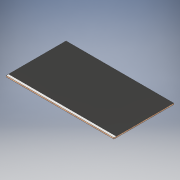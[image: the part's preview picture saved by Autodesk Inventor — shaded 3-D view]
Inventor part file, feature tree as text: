
AUTODESK INVENTOR PART (.ipt)
format: ipt  version: 2017 (Build 210142000, 142)  size: 102,400 bytes
history: native  units: in
note: dims shown in document units (in); Inventor stores cm internally (conversion verified against a paired STEP export)
features: extrude x2, sketch x2
ambient origin geometry x8: Origin, YZ Plane, XZ Plane, XY Plane, X Axis, Y Axis, Z Axis, Center Point
bodies: Solid1 (feature_tree)
feature tree (4):
  extrude  "Extrusion1"  Depth=25.0in
  extrude  "Extrusion2"  Depth=1.0in
  sketch  "Sketch1"  dims[d0=45.0in d1=25.0in]
  sketch  "Sketch2"  dims[d2=0.5in d3=0.0in d4=1.0in d5=0.001in d6=0.0in]
